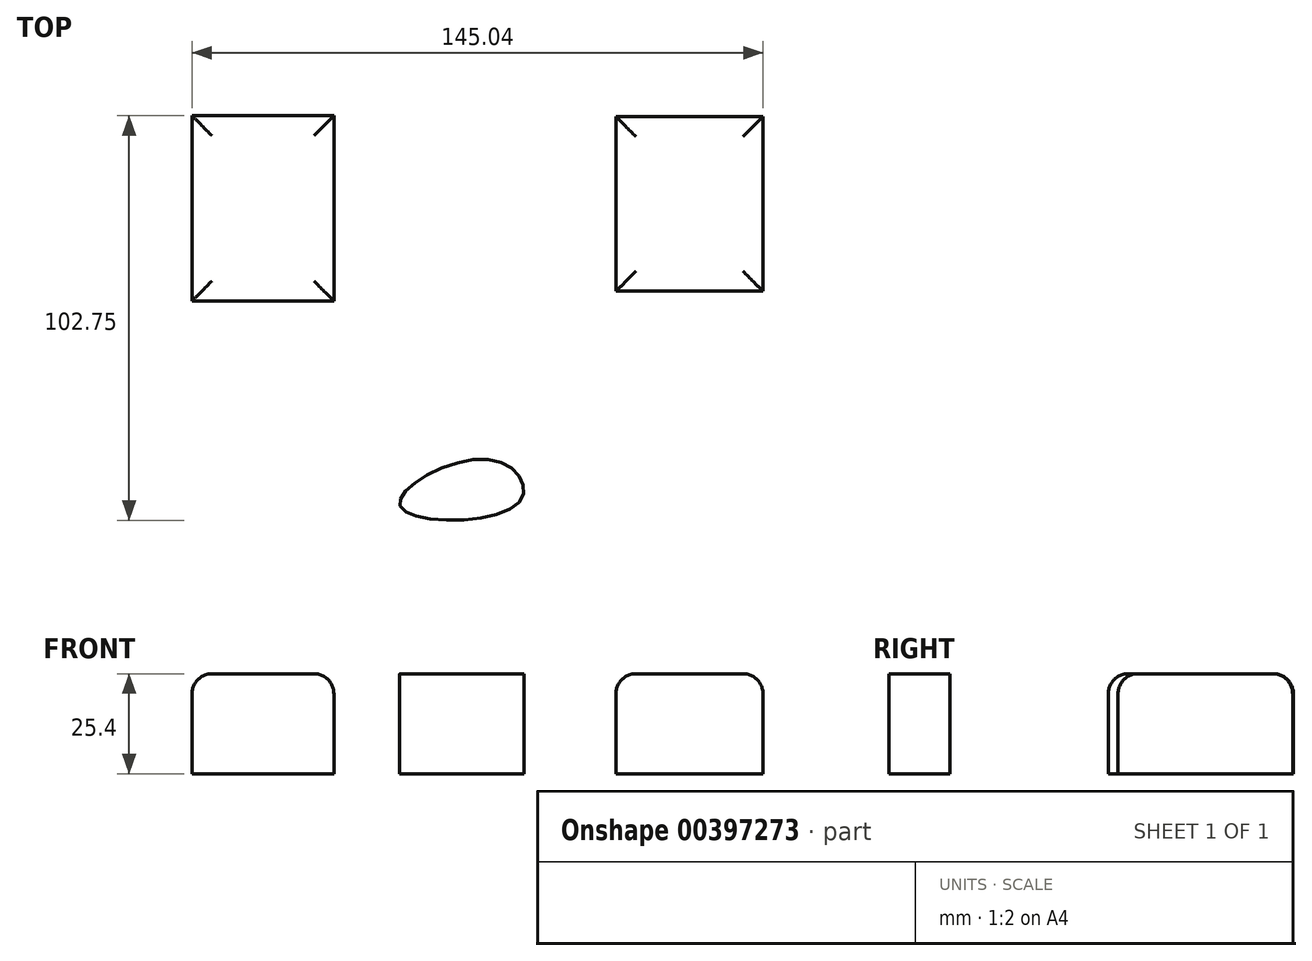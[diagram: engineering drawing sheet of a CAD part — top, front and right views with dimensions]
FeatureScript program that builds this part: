
annotation { "Feature Type Name" : "Feature", "Feature Type Description" : "" }
export const myFeature = defineFeature(function(context is Context, id is Id, definition is map)
    precondition{}
    {
        {
            var Q0;
            Q0=qCreatedBy(makeId("Top.planeOp"),FACE);
            var sketch = newSketch(context, id + "F0", { "sketchPlane" : qUnion([Q0])});
            skLineSegment(sketch, "E0.bottom", {"start": v(-73, 53.28) * mm, "end": v(-36.97, 53.28) * mm});
            skLineSegment(sketch, "E0.top", {"start": v(-73, 6.26) * mm, "end": v(-36.97, 6.26) * mm});
            skLineSegment(sketch, "E0.left", {"start": v(-73, 53.28) * mm, "end": v(-73, 6.26) * mm});
            skLineSegment(sketch, "E0.right", {"start": v(-36.97, 53.28) * mm, "end": v(-36.97, 6.26) * mm});
            skLineSegment(sketch, "E1.bottom", {"start": v(72.05, 53.09) * mm, "end": v(34.7, 53.09) * mm});
            skLineSegment(sketch, "E1.top", {"start": v(72.05, 8.72) * mm, "end": v(34.7, 8.72) * mm});
            skLineSegment(sketch, "E1.left", {"start": v(72.05, 53.09) * mm, "end": v(72.05, 8.72) * mm});
            skLineSegment(sketch, "E1.right", {"start": v(34.7, 53.09) * mm, "end": v(34.7, 8.72) * mm});
            skCircle(sketch, "E2", {"center": v(0, 0) * mm, "radius": 4.26 * mm});
            skFitSpline(sketch, "E3", {"points": [v(-20.1, -45.88) * mm, v(9.86, -45.12) * mm, v(3.22, -34.13) * mm, v(-20.1, -45.88) * mm]});
            skLineSegment(sketch, "E4.bottom", {"start": v(-76.22, 56.12) * mm, "end": v(76.03, 56.12) * mm});
            skLineSegment(sketch, "E4.top", {"start": v(-76.22, -56.12) * mm, "end": v(76.03, -56.12) * mm});
            skLineSegment(sketch, "E4.left", {"start": v(-76.22, 56.12) * mm, "end": v(-76.22, -56.12) * mm});
            skLineSegment(sketch, "E4.right", {"start": v(76.03, 56.12) * mm, "end": v(76.03, -56.12) * mm});
            skSolve(sketch);
        }
        {
            var Q0;
            Q0=makeQuery(id+"F0.imprint","IMPRINT",FACE,{"disambiguationData":[TD([[makeQuery(id+"F0.imprint","IMPRINT",EDGE,{"derivedFrom":sQuery(id+"F0.wireOp",EDGE,"E0.bottom")}),-1.0]])]});
            var Q1;
            Q1=makeQuery(id+"F0.imprint","IMPRINT",FACE,{"disambiguationData":[TD([[makeQuery(id+"F0.imprint","IMPRINT",EDGE,{"derivedFrom":sQuery(id+"F0.wireOp",EDGE,"E1.bottom")}),1.0]])]});
            var Q2;
            Q2=makeQuery(id+"F0.imprint","IMPRINT",FACE,{"disambiguationData":[TD([[makeQuery(id+"F0.imprint","IMPRINT",EDGE,{"derivedFrom":sQuery(id+"F0.wireOp",EDGE,"E3")}),1.0]])]});
            extrude(context, id + "F1", {"entities" : qUnion([Q0, Q1, Q2]), "depth" : 25.4 * mm});
        }
        {
            var Q0;
            Q0=makeQuery(id+"F1.opExtrude","CAP_EDGE",EDGE,{"disambiguationData":[OSD([sQuery(id+"F0.wireOp",EDGE,"E0.bottom")])],"isStart":false});
            var Q1;
            Q1=makeQuery(id+"F1.opExtrude","CAP_EDGE",EDGE,{"disambiguationData":[OSD([sQuery(id+"F0.wireOp",EDGE,"E0.left")])],"isStart":false});
            var Q2;
            Q2=makeQuery(id+"F1.opExtrude","CAP_EDGE",EDGE,{"disambiguationData":[OSD([sQuery(id+"F0.wireOp",EDGE,"E0.top")])],"isStart":false});
            var Q3;
            Q3=makeQuery(id+"F1.opExtrude","CAP_EDGE",EDGE,{"disambiguationData":[OSD([sQuery(id+"F0.wireOp",EDGE,"E0.right")])],"isStart":false});
            fillet(context, id + "F2", {"entities" : qUnion([Q0, Q1, Q2, Q3]), "radius" : 5.08 * mm, "tangentPropagation" : true, "allowEdgeOverflow" : false});
        }
        {
            var Q0;
            Q0=makeQuery(id+"F1.opExtrude","CAP_EDGE",EDGE,{"disambiguationData":[OSD([sQuery(id+"F0.wireOp",EDGE,"E1.bottom")])],"isStart":false});
            var Q1;
            Q1=makeQuery(id+"F1.opExtrude","CAP_EDGE",EDGE,{"disambiguationData":[OSD([sQuery(id+"F0.wireOp",EDGE,"E1.left")])],"isStart":false});
            var Q2;
            Q2=makeQuery(id+"F1.opExtrude","CAP_EDGE",EDGE,{"disambiguationData":[OSD([sQuery(id+"F0.wireOp",EDGE,"E1.top")])],"isStart":false});
            var Q3;
            Q3=makeQuery(id+"F1.opExtrude","CAP_EDGE",EDGE,{"disambiguationData":[OSD([sQuery(id+"F0.wireOp",EDGE,"E1.right")])],"isStart":false});
            fillet(context, id + "F3", {"entities" : qUnion([Q0, Q1, Q2, Q3]), "radius" : 5.08 * mm, "tangentPropagation" : true, "allowEdgeOverflow" : false});
        }
    });
